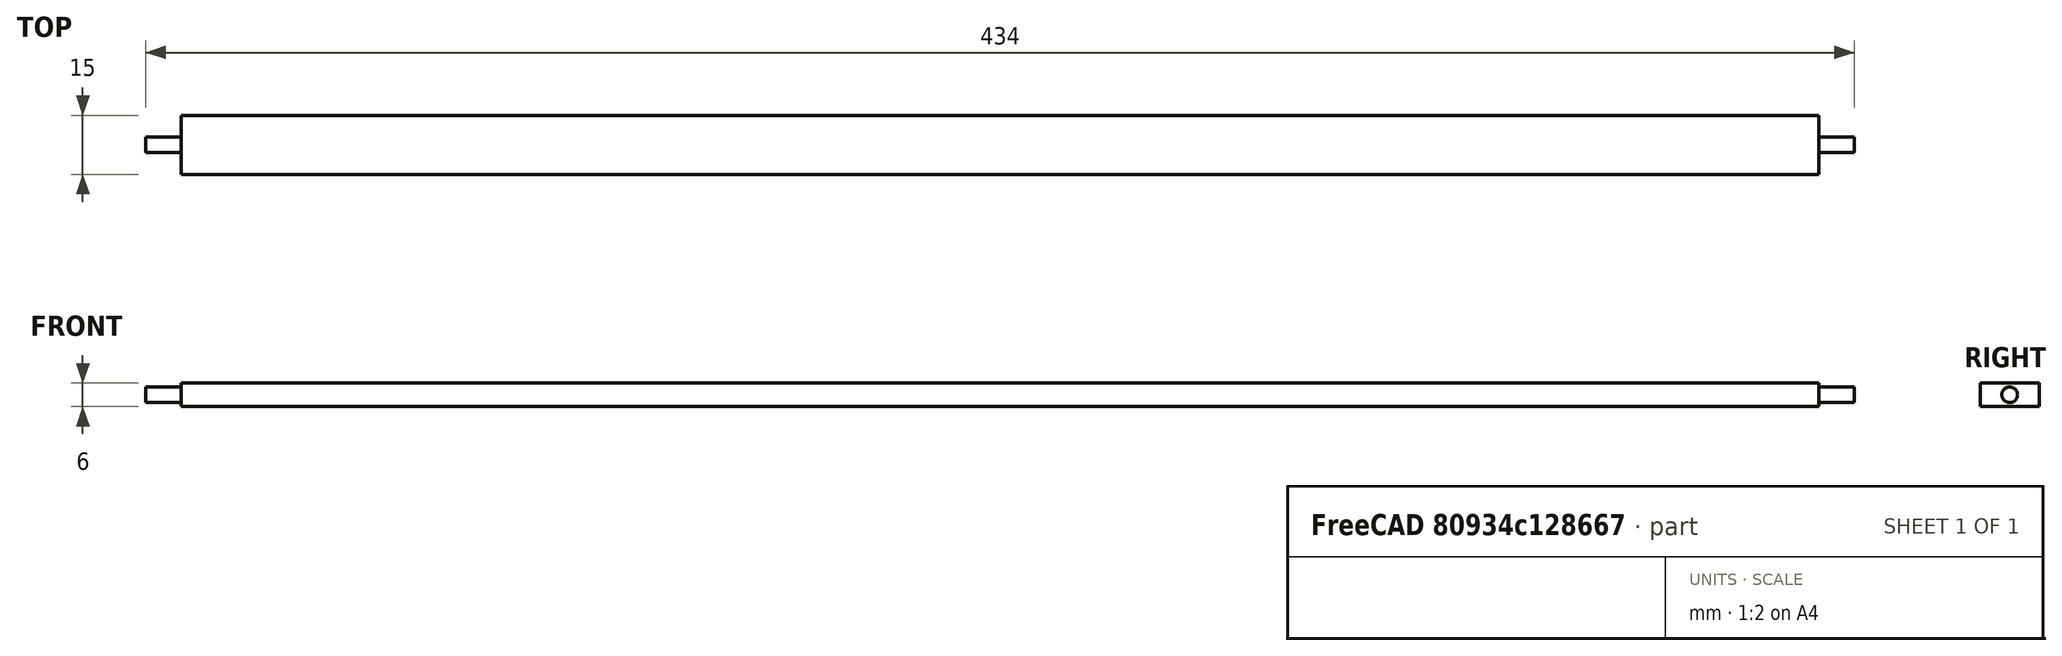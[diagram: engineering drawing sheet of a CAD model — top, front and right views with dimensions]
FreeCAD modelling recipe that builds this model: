
FCSTD DOCUMENT  (FreeCAD 1.0R39319 (Git))
Label: 17_lamella_back
License: All rights reserved
LicenseURL: http://en.wikipedia.org/wiki/All_rights_reserved
objects: TechDraw::DrawViewDimension×8, Sketcher::SketchObject×2, PartDesign::Pad×2, TechDraw::DrawProjGroupItem×2, TechDraw::DrawViewAnnotation×2, Spreadsheet::Sheet×1, PartDesign::Mirrored×1, PartDesign::Body×1, TechDraw::DrawSVGTemplate×1, TechDraw::DrawProjGroup×1, TechDraw::DrawViewBalloon×1, TechDraw::DrawPage×1
note: 23 computed .brp shape members not serialized (recipe doc carries the construction recipe); baked Part::Feature solids carry a one-line shape summary decoded from their .brp

FEATURE [Spreadsheet::Sheet] Spreadsheet
  cells = A4='length; B4(length)=416; A5='width; B5(width)=15; A6='height; B6(height)=6
FEATURE [Sketcher::SketchObject] Sketch
  ArcFitTolerance = 1e-06
  AttachmentSupport = -> [XY_Plane]
  FullyConstrained = true
  MakeInternals = false
  MapMode = 5
  expr: Constraints[11] = Spreadsheet.length
  expr: Constraints[12] = Spreadsheet.width
  sketch-geometry (5):
    g0: LineSegment StartX=-208 StartY=7.5 StartZ=0 EndX=-208 EndY=-7.5 EndZ=0
    g1: LineSegment StartX=-208 StartY=-7.5 StartZ=0 EndX=208 EndY=-7.5 EndZ=0
    g2: LineSegment StartX=208 StartY=-7.5 StartZ=0 EndX=208 EndY=7.5 EndZ=0
    g3: LineSegment StartX=208 StartY=7.5 StartZ=0 EndX=-208 EndY=7.5 EndZ=0
    g4: LineSegment [constr] StartX=-208 StartY=7.5 StartZ=0 EndX=208 EndY=-7.5 EndZ=0
  constraints (13):
    c: Coincident(g0,g1)
    c: Coincident(g1,g2)
    c: Coincident(g2,g3)
    c: Coincident(g3,g0)
    c: Vertical(g0)
    c: Vertical(g2)
    c: Horizontal(g1)
    c: Horizontal(g3)
    c: Coincident(g4,g0)
    c: Coincident(g4,g1)
    c: Symmetric(g4,g4,g-1)
    c: DistanceX(g3,g3) = 416
    c: DistanceY(g0,g0) = 15
FEATURE [PartDesign::Pad] Pad
  Direction = (0,0,1)
  Length = 6
  Length2 = 10
  Midplane = true
  Profile = -> Sketch
  ReferenceAxis = -> Sketch [N_Axis]
  Suppressed = false
  Type = 0
  expr: Length = Spreadsheet.height
FEATURE [Sketcher::SketchObject] Sketch001
  ArcFitTolerance = 1e-06
  AttachmentSupport = -> [Pad]
  ExternalGeometry = -> [Pad]
  FullyConstrained = true
  MakeInternals = false
  MapMode = 5
  Placement = pos=(208,0,0) rot=(0.57735,0.57735,0.57735;2.0944rad)
  sketch-geometry (1):
    g0: Circle CenterX=0 CenterY=0 CenterZ=0 NormalX=0 NormalY=0 NormalZ=1 AngleXU=0 Radius=2
  constraints (3):
    c: Coincident(g0,g-1)
    c: Diameter(g0) = 4
    c: DistanceY(g-3,g-3) = 6
FEATURE [PartDesign::Pad] Pad001
  BaseFeature = -> Pad
  Direction = (1,0,0)
  Length = 9
  Length2 = 10
  Profile = -> Sketch001
  ReferenceAxis = -> Sketch001 [N_Axis]
  Suppressed = false
  Type = 0
FEATURE [PartDesign::Mirrored] Mirrored
  BaseFeature = -> Pad001
  MirrorPlane = -> YZ_Plane
  Originals = -> [Pad001]
  Suppressed = false
  TransformMode = 0
FEATURE [PartDesign::Body] Body
  AllowCompound = false
  Group = -> [Sketch,Pad,Sketch001,Pad001,Mirrored]
  Origin = -> Origin
  Tip = -> Mirrored
FEATURE [TechDraw::DrawSVGTemplate] Template
  EditableTexts = AuthorName=Matthias Mosimann; CheckDate=N/A; CreationDate=11/04/2026; DrawingNumber=1.0; FC-Title=Lamellen Rücken; SheetNumber=1 / 1; SupervisorName=N/A; Weight=N/A; scale=1 : 2
  Height = 297
  Orientation = 1
  Template = C:/Program Files/FreeCAD 1.0/data/Mod/TechDraw/Templates/A3_Landscape_TD.svg
  Width = 420
FEATURE [TechDraw::DrawProjGroupItem] View  label="Front"
  CoarseView = false
  Direction = (-1,0,1e-16)
  Focus = 100
  HardHidden = false
  IsoCount = 0
  IsoHidden = false
  IsoVisible = false
  LockPosition = true
  Perspective = false
  Rotation = 0
  RotationVector = (1,0,0)
  Scale = 0.5
  ScaleType = 2
  ScrubCount = 1
  SeamHidden = false
  SeamVisible = true
  SmoothHidden = false
  SmoothVisible = true
  Source = -> [Body]
  Type = 0
  X = 0
  XDirection = (0,-1,1e-16)
  Y = 0
FEATURE [TechDraw::DrawProjGroupItem] ProjItem  label="Left"
  CoarseView = false
  Direction = (-1e-16,1,-1e-16)
  Focus = 100
  HardHidden = false
  IsoCount = 0
  IsoHidden = false
  IsoVisible = false
  LockPosition = true
  Perspective = false
  Rotation = 0
  RotationVector = (1,0,0)
  Scale = 0.5
  ScaleType = 2
  ScrubCount = 1
  SeamHidden = false
  SeamVisible = true
  SmoothHidden = false
  SmoothVisible = true
  Source = -> [Body]
  Type = 1
  X = 141.25
  XDirection = (-1,-1e-16,1e-16)
  Y = 0
FEATURE [TechDraw::DrawProjGroup] ProjGroup
  Anchor = -> View
  AutoDistribute = true
  LockPosition = false
  ProjectionType = 0
  Rotation = 0
  Scale = 0.5
  ScaleType = 2
  Source = -> [Body]
  Views = -> [View,ProjItem]
  X = 76.3032
  Y = 163.571
  spacingX = 30
  spacingY = 30
FEATURE [TechDraw::DrawViewDimension] Dimension
  AngleOverride = false
  Arbitrary = false
  ArbitraryTolerances = false
  BoxCorners = (2) [(-107.5,-1.5,-1e-07),(107.5,1.5,1e-07)]
  EqualTolerance = true
  ExtensionAngle = 0
  FormatSpec = %.2w
  FormatSpecOverTolerance = %+.2w
  FormatSpecUnderTolerance = %+.2w
  Inverted = false
  LineAngle = 0
  LockPosition = false
  MeasureType = 1
  OverTolerance = 0
  References2D = -> [ProjItem]
  Rotation = 0
  ScaleType = 0
  TheoreticalExact = false
  Type = 1
  UnderTolerance = 0
  X = 0
  Y = 20.3682
FEATURE [TechDraw::DrawViewDimension] Dimension001
  AngleOverride = false
  Arbitrary = false
  ArbitraryTolerances = false
  BoxCorners = (2) [(-3.75,-1.5,0),(3.75,1.5,0)]
  EqualTolerance = true
  ExtensionAngle = 0
  FormatSpec = %.2w
  FormatSpecOverTolerance = %+.2w
  FormatSpecUnderTolerance = %+.2w
  Inverted = false
  LineAngle = 0
  LockPosition = false
  MeasureType = 1
  OverTolerance = 0
  References2D = -> [View]
  Rotation = 0
  ScaleType = 0
  TheoreticalExact = false
  Type = 0
  UnderTolerance = 0
  X = -23.7903
  Y = -5.26475
FEATURE [TechDraw::DrawViewDimension] Dimension002
  AngleOverride = false
  Arbitrary = false
  ArbitraryTolerances = false
  BoxCorners = (2) [(-3.75,-1.5,0),(3.75,1.5,0)]
  EqualTolerance = true
  ExtensionAngle = 0
  FormatSpec = ⌀%.2w
  FormatSpecOverTolerance = %+.2w
  FormatSpecUnderTolerance = %+.2w
  Inverted = false
  LineAngle = 0
  LockPosition = false
  MeasureType = 1
  OverTolerance = 0
  References2D = -> [View]
  Rotation = 0
  ScaleType = 0
  TheoreticalExact = false
  Type = 5
  UnderTolerance = 0
  X = 17.1049
  Y = 11.5879
FEATURE [TechDraw::DrawViewDimension] Dimension003
  AngleOverride = false
  Arbitrary = false
  ArbitraryTolerances = false
  BoxCorners = (2) [(-107.5,-1.5,-1e-07),(107.5,1.5,1e-07)]
  EqualTolerance = true
  ExtensionAngle = 0
  FormatSpec = %.2w
  FormatSpecOverTolerance = %+.2w
  FormatSpecUnderTolerance = %+.2w
  Inverted = false
  LineAngle = 0
  LockPosition = false
  MeasureType = 1
  OverTolerance = 0
  References2D = -> [ProjItem]
  Rotation = 0
  ScaleType = 0
  TheoreticalExact = false
  Type = 0
  UnderTolerance = 0
  X = -115.167
  Y = 20.3682
FEATURE [TechDraw::DrawViewDimension] Dimension004
  AngleOverride = false
  Arbitrary = false
  ArbitraryTolerances = false
  BoxCorners = (2) [(-107.5,-1.5,-1e-07),(107.5,1.5,1e-07)]
  EqualTolerance = true
  ExtensionAngle = 0
  FormatSpec = %.2w
  FormatSpecOverTolerance = %+.2w
  FormatSpecUnderTolerance = %+.2w
  Inverted = false
  LineAngle = 0
  LockPosition = false
  MeasureType = 1
  OverTolerance = 0
  References2D = -> [ProjItem]
  Rotation = 0
  ScaleType = 0
  TheoreticalExact = false
  Type = 0
  UnderTolerance = 0
  X = 123.742
  Y = 20.3682
FEATURE [TechDraw::DrawViewDimension] Dimension005
  AngleOverride = false
  Arbitrary = false
  ArbitraryTolerances = false
  BoxCorners = (2) [(-3.75,-1.5,0),(3.75,1.5,0)]
  EqualTolerance = true
  ExtensionAngle = 0
  FormatSpec = %.2w
  FormatSpecOverTolerance = %+.2w
  FormatSpecUnderTolerance = %+.2w
  Inverted = false
  LineAngle = 0
  LockPosition = false
  MeasureType = 1
  OverTolerance = 0
  References2D = -> [View]
  Rotation = 0
  ScaleType = 0
  TheoreticalExact = false
  Type = 0
  UnderTolerance = 0
  X = 2.63958
  Y = -12.4273
FEATURE [TechDraw::DrawViewDimension] Dimension006
  AngleOverride = false
  Arbitrary = false
  ArbitraryTolerances = false
  BoxCorners = (2) [(-3.75,-1.5,0),(3.75,1.5,0)]
  EqualTolerance = true
  ExtensionAngle = 0
  FormatSpec = %.2w
  FormatSpecOverTolerance = %+.2w
  FormatSpecUnderTolerance = %+.2w
  Inverted = false
  LineAngle = 0
  LockPosition = false
  MeasureType = 1
  OverTolerance = 0
  References2D = -> [View]
  Rotation = 0
  ScaleType = 0
  TheoreticalExact = false
  Type = 0
  UnderTolerance = 0
  X = -11.6553
  Y = 15.9621
FEATURE [TechDraw::DrawViewDimension] Dimension007
  AngleOverride = false
  Arbitrary = false
  ArbitraryTolerances = false
  BoxCorners = (2) [(-3.75,-1.5,0),(3.75,1.5,0)]
  EqualTolerance = true
  ExtensionAngle = 0
  FormatSpec = %.2w
  FormatSpecOverTolerance = %+.2w
  FormatSpecUnderTolerance = %+.2w
  Inverted = false
  LineAngle = 0
  LockPosition = false
  MeasureType = 1
  OverTolerance = 0
  References2D = -> [View]
  Rotation = 0
  ScaleType = 0
  TheoreticalExact = false
  Type = 0
  UnderTolerance = 0
  X = -18.2186
  Y = -15.4903
FEATURE [TechDraw::DrawViewAnnotation] Annotation005
  Font = osifont
  LineSpace = 80
  LockPosition = false
  MaxWidth = 120
  Rotation = 0
  Scale = 0.75
  ScaleType = 1
  Text = Teil wird aus standard Stahlprofil hergestellt 15mm x 6mm. Achtung! Stifte müssen aus Edelstahl 4mm sein. Alle Angaben in mm. 3D Ansichten können von der angegebenen Skalierungsgrösse abweichen.
  TextSize = 3
  TextStyle = 1
  X = 118.975
  Y = 263.388
FEATURE [TechDraw::DrawViewBalloon] Balloon
  BubbleShape = 0
  EndType = 0
  EndTypeScale = 1
  KinkLength = 5
  LockPosition = false
  OriginX = -211.5
  OriginY = 2
  Rotation = 0
  ScaleType = 0
  ShapeScale = 1
  SourceView = -> ProjItem
  Text = 1
  TextWrapLen = -1
  X = -137.731
  Y = 51.6482
FEATURE [TechDraw::DrawViewAnnotation] Annotation
  Font = osifont
  LineSpace = 80
  LockPosition = false
  MaxWidth = 120
  Rotation = 0
  ScaleType = 0
  Text = (1) Stifte sind aus Edelstahl. 9mm müssen auf einer Seite unbedingt eingehalten werden, weil die Lamellen in einem 4.1mm Sacklock in der Edelstahlhülse frei beweglich sein müssen und aufstehen.!
  TextSize = 3
  TextStyle = 0
  X = 118.975
  Y = 223.301
FEATURE [TechDraw::DrawPage] Page
  KeepUpdated = true
  NextBalloonIndex = 2
  ProjectionType = 0
  Template = -> Template
  Views = -> [ProjGroup,Dimension,Dimension001,Dimension002,Dimension003,Dimension004,Dimension005,Dimension006,Dimension007,Annotation005,Balloon,Annotation]
